# Revit family: Lockin Lockers AU_DDA Accessible Locker_R22
name_source: partatom
category: Furniture
units: mm (PartAtom-declared; Revit-internal decimal feet)

## family parameters
Always vertical = Yes
Cut with Voids When Loaded = No
OmniClass Number = 23.40.20.27
OmniClass Title = Storage Shelving
Render Appearance Source = Family Geometry
Room Calculation Point = No
Shared = Yes
Work Plane-Based = Yes

## types (8) — shared parameters
Body/Frame Material = Material - Melamine - Laminex or Polytec Finish
DDA Door Type = Lockin_Locker Door_Standard_R22 : DDA Door/Combination Lock
Desired Width = 400 mm  [stored 1.31234 ft]
Door Material = Material - Melamine - Laminex or Polytec Finish
Door Type = Lockin_Locker Door_Standard_R22 : Standard Door/Combination Lock
Locker Joint = 3 mm  [stored 0.00984252 ft]
Manufacturer = Lockin Lockers AU
Maximum Base Height = 450 mm  [stored 1.47638 ft]
Maximum Depth = 550 mm
Maximum Width = 500 mm  [stored 1.64042 ft]
Minimum Base Height = 100 mm  [stored 0.328084 ft]
Minimum Depth = 400 mm  [stored 1.31234 ft]
Minimum Width = 400 mm  [stored 1.31234 ft]
TH Wall = 18 mm  [stored 0.0590551 ft]
URL = https://www.lockin.com.au
Width Control = 400 mm  [stored 1.31234 ft]
zero-valued in all types: Default Elevation

## per-type parameters (varying)
- DDA Locker 1 door - Hanging (ALP1): ALPS2 Doors=No; Base Height Control=450 mm  [stored 1.47638 ft]; Base Height Offset=450 mm  [stored 1.47638 ft]; Depth Control=550 mm; Description=DDA Locker 1 door - Hanging; Desired Base Height=450 mm  [stored 1.47638 ft]; Desired Depth=550 mm; Desired Height=1350 mm  [stored 4.42913 ft]; H ALPS2 Locker DDA=900 mm  [stored 2.95276 ft]; H ALPS2 Locker Std=603 mm; H Locker=900 mm  [stored 2.95276 ft]; Height Control=1350 mm  [stored 4.42913 ft]; Maximum Height=1350 mm  [stored 4.42913 ft]; Minimum Height=1350 mm  [stored 4.42913 ft]; Model=ALP1; N_Doors=1; No Shoe Box=Yes; Offset DDA Locker=0 mm  [stored 0 ft]; Shoe Box=No; Standard Doors=Yes; vis_Coatrack Bottom=No; vis_Coatrack Top=Yes; vis_Shelf 1=No; vis_Shelf 2=No; vis_Shelf 3=No; vis_Shelf 4=No; vis_Shelves ALH1=No; vis_Std Locker 1=No; vis_Std Locker 2=No; vis_Std Locker 3=No; vis_Std Locker 4=No; vis_Std Locker 5=No
- DDA Locker 2 door - Hanging (ALP2): ALPS2 Doors=No; Base Height Control=100 mm  [stored 0.328084 ft]; Base Height Offset=100 mm  [stored 0.328084 ft]; Depth Control=550 mm; Description=DDA Locker 2 door - Hanging; Desired Base Height=100 mm  [stored 0.328084 ft]; Desired Depth=550 mm; Desired Height=1900 mm  [stored 6.2336 ft]; H ALPS2 Locker DDA=898.5 mm  [stored 2.94783 ft]; H ALPS2 Locker Std=1203.99 mm  [stored 3.9501 ft]; H Locker=898.5 mm  [stored 2.94783 ft]; Height Control=1900 mm  [stored 6.2336 ft]; Maximum Height=2100 mm; Minimum Height=1800 mm  [stored 5.90551 ft]; Model=ALP2; N_Doors=2; No Shoe Box=Yes; Offset DDA Locker=0 mm  [stored 0 ft]; Shoe Box=No; Standard Doors=Yes; vis_Coatrack Bottom=Yes; vis_Coatrack Top=Yes; vis_Shelf 1=Yes; vis_Shelf 2=No; vis_Shelf 3=No; vis_Shelf 4=No; vis_Shelves ALH1=No; vis_Std Locker 1=No; vis_Std Locker 2=Yes; vis_Std Locker 3=No; vis_Std Locker 4=No; vis_Std Locker 5=No
- DDA Locker 2 door - Hanging/Shelf (ALPS2): ALPS2 Doors=Yes; Base Height Control=450 mm  [stored 1.47638 ft]; Base Height Offset=450 mm  [stored 1.47638 ft]; Depth Control=550 mm; Description=DDA Locker 2 door - Hanging/Shelf; Desired Base Height=450 mm  [stored 1.47638 ft]; Desired Depth=550 mm; Desired Height=1900 mm  [stored 6.2336 ft]; H ALPS2 Locker DDA=477.51 mm  [stored 1.56663 ft]; H ALPS2 Locker Std=969.49 mm  [stored 3.18074 ft]; H Locker=723.5 mm  [stored 2.37369 ft]; Height Control=1900 mm  [stored 6.2336 ft]; Maximum Height=2100 mm; Minimum Height=1800 mm  [stored 5.90551 ft]; Model=ALPS2; N_Doors=2; No Shoe Box=Yes; Offset DDA Locker=0 mm  [stored 0 ft]; Shoe Box=No; Standard Doors=No; vis_Coatrack Bottom=No; vis_Coatrack Top=Yes; vis_Shelf 1=No; vis_Shelf 2=No; vis_Shelf 3=No; vis_Shelf 4=No; vis_Shelves ALH1=No; vis_Std Locker 1=No; vis_Std Locker 2=No; vis_Std Locker 3=No; vis_Std Locker 4=No; vis_Std Locker 5=No
- DDA Locker 2 door - Hanging w. s/box (ALPB2): ALPS2 Doors=No; Base Height Control=450 mm  [stored 1.47638 ft]; Base Height Offset=100 mm  [stored 0.328084 ft]; Depth Control=550 mm; Description=DDA Locker 2 door - Hanging w. s/box; Desired Base Height=450 mm  [stored 1.47638 ft]; Desired Depth=550 mm; Desired Height=1900 mm  [stored 6.2336 ft]; H ALPS2 Locker DDA=723.5 mm  [stored 2.37369 ft]; H ALPS2 Locker Std=969.49 mm  [stored 3.18074 ft]; H Locker=723.5 mm  [stored 2.37369 ft]; Height Control=1900 mm  [stored 6.2336 ft]; Maximum Height=2100 mm; Minimum Height=1800 mm  [stored 5.90551 ft]; Model=ALPB2; N_Doors=2; No Shoe Box=No; Offset DDA Locker=0 mm  [stored 0 ft]; Shoe Box=Yes; Standard Doors=Yes; vis_Coatrack Bottom=Yes; vis_Coatrack Top=Yes; vis_Shelf 1=Yes; vis_Shelf 2=No; vis_Shelf 3=No; vis_Shelf 4=No; vis_Shelves ALH1=No; vis_Std Locker 1=No; vis_Std Locker 2=Yes; vis_Std Locker 3=No; vis_Std Locker 4=No; vis_Std Locker 5=No
- DDA Locker 1 door - shelves (ALH1): ALPS2 Doors=No; Base Height Control=450 mm  [stored 1.47638 ft]; Base Height Offset=450 mm  [stored 1.47638 ft]; Depth Control=400 mm  [stored 1.31234 ft]; Description=DDA Locker 1 door - shelves; Desired Base Height=450 mm  [stored 1.47638 ft]; Desired Depth=400 mm  [stored 1.31234 ft]; Desired Height=1350 mm  [stored 4.42913 ft]; H ALPS2 Locker DDA=900 mm  [stored 2.95276 ft]; H ALPS2 Locker Std=603 mm; H Locker=900 mm  [stored 2.95276 ft]; Height Control=1350 mm  [stored 4.42913 ft]; Maximum Height=1350 mm  [stored 4.42913 ft]; Minimum Height=1350 mm  [stored 4.42913 ft]; Model=ALH1; N_Doors=1; No Shoe Box=Yes; Offset DDA Locker=0 mm  [stored 0 ft]; Shoe Box=No; Standard Doors=Yes; vis_Coatrack Bottom=No; vis_Coatrack Top=No; vis_Shelf 1=No; vis_Shelf 2=No; vis_Shelf 3=No; vis_Shelf 4=No; vis_Shelves ALH1=Yes; vis_Std Locker 1=No; vis_Std Locker 2=No; vis_Std Locker 3=No; vis_Std Locker 4=No; vis_Std Locker 5=No
- DDA Locker 3 door - shelves (ALH3): ALPS2 Doors=No; Base Height Control=200 mm  [stored 0.656168 ft]; Base Height Offset=200 mm  [stored 0.656168 ft]; Depth Control=550 mm; Description=DDA Locker 3 door - shelves; Desired Base Height=200 mm  [stored 0.656168 ft]; Desired Depth=550 mm; Desired Height=1900 mm  [stored 6.2336 ft]; H ALPS2 Locker DDA=564.67 mm; H ALPS2 Locker Std=1134.98 mm  [stored 3.72369 ft]; H Locker=564.67 mm; Height Control=1900 mm  [stored 6.2336 ft]; Maximum Height=2100 mm; Minimum Height=1800 mm  [stored 5.90551 ft]; Model=ALH3; N_Doors=3; No Shoe Box=Yes; Offset DDA Locker=567.67 mm; Shoe Box=No; Standard Doors=Yes; vis_Coatrack Bottom=No; vis_Coatrack Top=No; vis_Shelf 1=Yes; vis_Shelf 2=Yes; vis_Shelf 3=No; vis_Shelf 4=No; vis_Shelves ALH1=No; vis_Std Locker 1=Yes; vis_Std Locker 2=No; vis_Std Locker 3=Yes; vis_Std Locker 4=No; vis_Std Locker 5=No
- DDA Locker 4 door - shelves (ALH4): ALPS2 Doors=No; Base Height Control=200 mm  [stored 0.656168 ft]; Base Height Offset=200 mm  [stored 0.656168 ft]; Depth Control=550 mm; Description=DDA Locker 4 door - shelves; Desired Base Height=200 mm  [stored 0.656168 ft]; Desired Depth=550 mm; Desired Height=1900 mm  [stored 6.2336 ft]; H ALPS2 Locker DDA=422.75 mm  [stored 1.38698 ft]; H ALPS2 Locker Std=1132.97 mm; H Locker=422.75 mm  [stored 1.38698 ft]; Height Control=1900 mm  [stored 6.2336 ft]; Maximum Height=2100 mm; Minimum Height=1800 mm  [stored 5.90551 ft]; Model=ALH4; N_Doors=4; No Shoe Box=Yes; Offset DDA Locker=425.75 mm  [stored 1.39682 ft]; Shoe Box=No; Standard Doors=Yes; vis_Coatrack Bottom=No; vis_Coatrack Top=No; vis_Shelf 1=Yes; vis_Shelf 2=Yes; vis_Shelf 3=Yes; vis_Shelf 4=No; vis_Shelves ALH1=No; vis_Std Locker 1=Yes; vis_Std Locker 2=No; vis_Std Locker 3=Yes; vis_Std Locker 4=Yes; vis_Std Locker 5=No
- DDA Locker 5 door - shelves (ALH5): ALPS2 Doors=No; Base Height Control=200 mm  [stored 0.656168 ft]; Base Height Offset=200 mm  [stored 0.656168 ft]; Depth Control=550 mm; Description=DDA Locker 5 door - shelves; Desired Base Height=200 mm  [stored 0.656168 ft]; Desired Depth=550 mm; Desired Height=1900 mm  [stored 6.2336 ft]; H ALPS2 Locker DDA=337.6 mm  [stored 1.10761 ft]; H ALPS2 Locker Std=1130.96 mm  [stored 3.7105 ft]; H Locker=337.6 mm  [stored 1.10761 ft]; Height Control=1900 mm  [stored 6.2336 ft]; Maximum Height=2100 mm; Minimum Height=1800 mm  [stored 5.90551 ft]; Model=ALH5; N_Doors=5; No Shoe Box=Yes; Offset DDA Locker=681.2 mm; Shoe Box=No; Standard Doors=Yes; vis_Coatrack Bottom=No; vis_Coatrack Top=No; vis_Shelf 1=Yes; vis_Shelf 2=Yes; vis_Shelf 3=Yes; vis_Shelf 4=Yes; vis_Shelves ALH1=No; vis_Std Locker 1=Yes; vis_Std Locker 2=Yes; vis_Std Locker 3=No; vis_Std Locker 4=Yes; vis_Std Locker 5=Yes

note: [stored X ft] marks values corroborated as IEEE doubles in the binary element streams (Revit-internal decimal feet)

## geometry (parser evidence)
native form markers: Sweep x5
no freeform markers — native parametric forms only
